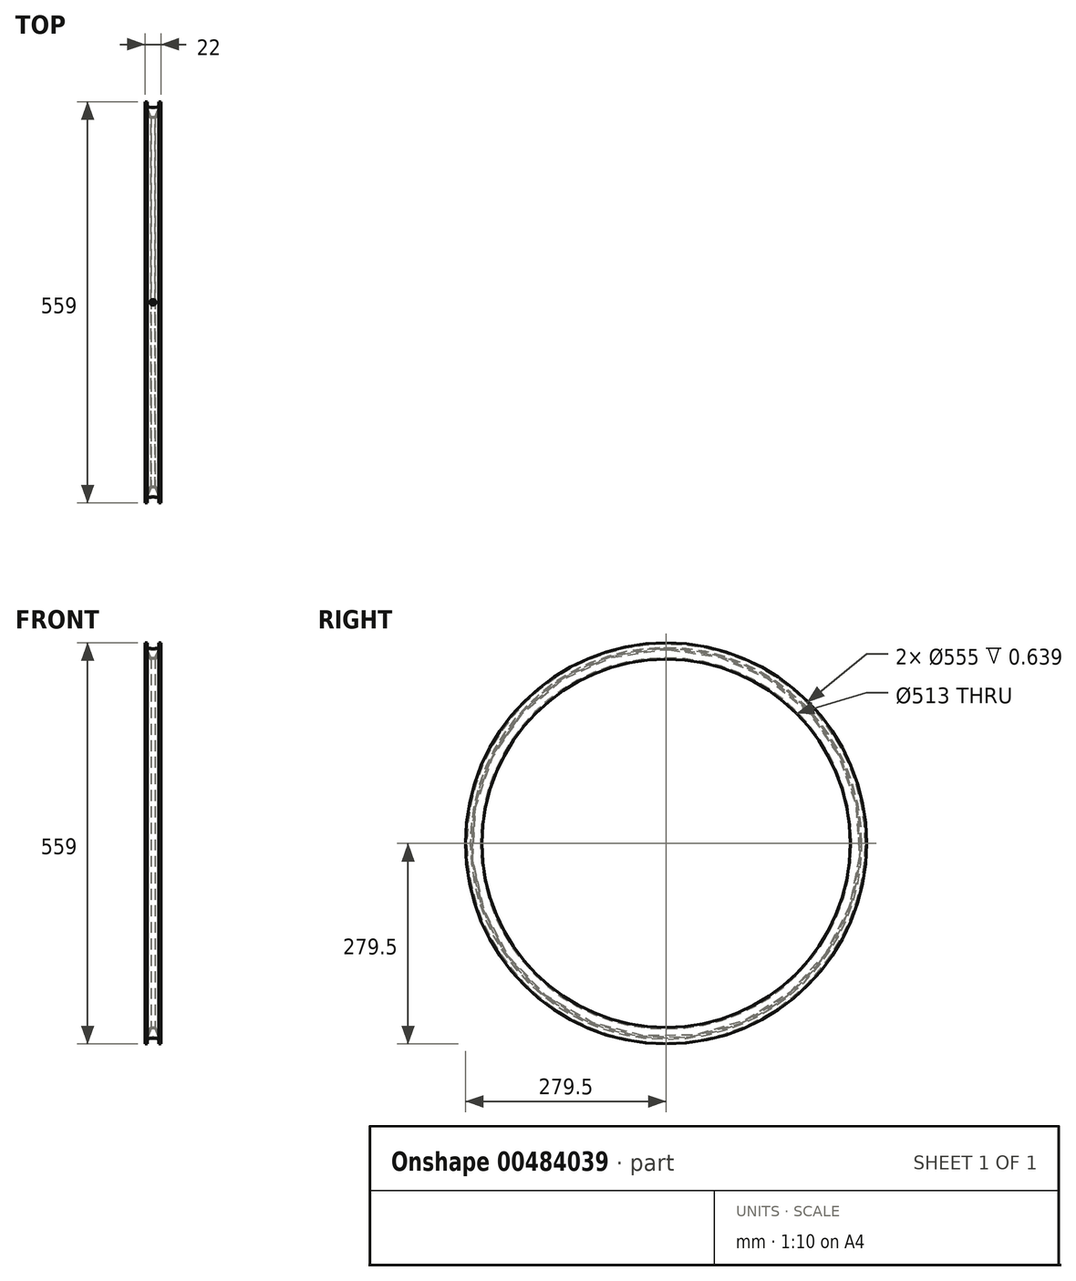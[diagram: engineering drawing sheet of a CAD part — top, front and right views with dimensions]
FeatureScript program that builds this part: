
annotation { "Feature Type Name" : "Feature", "Feature Type Description" : "" }
export const myFeature = defineFeature(function(context is Context, id is Id, definition is map)
    precondition{}
    {
        {
            var Q0;
            Q0=qCreatedBy(makeId("Front.planeOp"),FACE);
            var sketch = newSketch(context, id + "F0", { "sketchPlane" : qUnion([Q0])});
            skLineSegment(sketch, "E0", {"start": v(0, 0) * mm, "end": v(32.12, 0) * mm, "construction": true});
            skLineSegment(sketch, "E1", {"start": v(-11, 279.5) * mm, "end": v(-8, 279.5) * mm});
            skLineSegment(sketch, "E2", {"start": v(0, 279.5) * mm, "end": v(0, 0) * mm, "construction": true});
            skLineSegment(sketch, "E3", {"start": v(-11, 279.5) * mm, "end": v(-9.1, 268.15) * mm});
            skLineSegment(sketch, "E4", {"start": v(-8.73, 266.9) * mm, "end": v(-4.53, 257.67) * mm});
            skLineSegment(sketch, "E5", {"start": v(-2.71, 256.5) * mm, "end": v(2.71, 256.5) * mm});
            skLineSegment(sketch, "E6", {"start": v(4.53, 257.67) * mm, "end": v(8.73, 266.9) * mm});
            skLineSegment(sketch, "E7", {"start": v(9.1, 268.15) * mm, "end": v(11, 279.5) * mm});
            skPoint(sketch, "E8.visualSharp", {"position": v(-9, 267.5) * mm});
            skArc(sketch, "E8.filletArc", {"start": v(-9.1, 268.15) * mm, "mid": v(-8.96, 267.51) * mm, "end": v(-8.73, 266.9) * mm});
            skPoint(sketch, "E9.visualSharp", {"position": v(9, 267.5) * mm});
            skArc(sketch, "E9.filletArc", {"start": v(8.73, 266.9) * mm, "mid": v(8.96, 267.51) * mm, "end": v(9.1, 268.15) * mm});
            skPoint(sketch, "E10.visualSharp", {"position": v(-4, 256.5) * mm});
            skArc(sketch, "E10.filletArc", {"start": v(-4.53, 257.67) * mm, "mid": v(-3.8, 256.82) * mm, "end": v(-2.71, 256.5) * mm});
            skPoint(sketch, "E11.visualSharp", {"position": v(4, 256.5) * mm});
            skArc(sketch, "E11.filletArc", {"start": v(2.71, 256.5) * mm, "mid": v(3.8, 256.82) * mm, "end": v(4.53, 257.67) * mm});
            skLineSegment(sketch, "E12.0", {"start": v(-8.64, 277.5) * mm, "end": v(-8, 277.5) * mm});
            skLineSegment(sketch, "E12.1", {"start": v(7.14, 268.48) * mm, "end": v(7.57, 271.1) * mm});
            skLineSegment(sketch, "E12.2", {"start": v(-8.64, 277.5) * mm, "end": v(-7.85, 272.76) * mm});
            skArc(sketch, "E12.3", {"start": v(6.9, 267.73) * mm, "mid": v(7.05, 268.1) * mm, "end": v(7.14, 268.48) * mm});
            skLineSegment(sketch, "E12.4", {"start": v(2.71, 258.5) * mm, "end": v(6.9, 267.73) * mm});
            skLineSegment(sketch, "E12.5", {"start": v(2.71, 258.5) * mm, "end": v(2.71, 258.5) * mm});
            skArc(sketch, "E12.6", {"start": v(-7.14, 268.48) * mm, "mid": v(-7.05, 268.1) * mm, "end": v(-6.9, 267.73) * mm});
            skLineSegment(sketch, "E12.7", {"start": v(-6.9, 267.73) * mm, "end": v(-2.71, 258.5) * mm});
            skLineSegment(sketch, "E12.8", {"start": v(-2.71, 258.5) * mm, "end": v(-2.71, 258.5) * mm});
            skLineSegment(sketch, "E12.9", {"start": v(-2.71, 258.5) * mm, "end": v(2.71, 258.5) * mm});
            skLineSegment(sketch, "E13", {"start": v(-8, 279.5) * mm, "end": v(-8, 277.5) * mm});
            skLineSegment(sketch, "E14", {"start": v(8, 279.5) * mm, "end": v(8, 277.5) * mm});
            skLineSegment(sketch, "E15.trimOffspring", {"start": v(8, 279.5) * mm, "end": v(11, 279.5) * mm});
            skLineSegment(sketch, "E16.trimOffspring", {"start": v(8, 277.5) * mm, "end": v(8.64, 277.5) * mm});
            skArc(sketch, "E17", {"start": v(-7.85, 272.76) * mm, "mid": v(0, 271.5) * mm, "end": v(7.85, 272.76) * mm});
            skArc(sketch, "E18", {"start": v(-7.57, 271.1) * mm, "mid": v(0, 270) * mm, "end": v(7.57, 271.1) * mm});
            skLineSegment(sketch, "E19.trimOffspring", {"start": v(7.85, 272.76) * mm, "end": v(8.64, 277.5) * mm});
            skLineSegment(sketch, "E20.trimOffspring", {"start": v(-7.57, 271.1) * mm, "end": v(-7.14, 268.48) * mm});
            skSolve(sketch);
        }
        {
            var Q0;
            Q0 = qSketchRegion(id + "F0", true);
            var Q1;
            Q1=sQuery(id+"F0.wireOp",EDGE,"E0");
            revolve(context, id + "F1", {"entities" : qUnion([Q0]), "axis" : qUnion([Q1]), "revolveType" : RevolveType.FULL});
        }
        {
            var Q0;
            Q0=qCreatedBy(makeId("Front.planeOp"),FACE);
            var sketch = newSketch(context, id + "F2", { "sketchPlane" : qUnion([Q0])});
            skLineSegment(sketch, "E21.bottom", {"start": v(0, 250) * mm, "end": v(-2, 250) * mm});
            skLineSegment(sketch, "E21.left", {"start": v(0, 250) * mm, "end": v(0, 265) * mm});
            skLineSegment(sketch, "E21.right", {"start": v(-2, 250) * mm, "end": v(-2, 265) * mm});
            skLineSegment(sketch, "E22.bottom", {"start": v(-2, 265) * mm, "end": v(-4, 265) * mm});
            skLineSegment(sketch, "E22.top", {"start": v(0, 275) * mm, "end": v(-4, 275) * mm});
            skLineSegment(sketch, "E22.left", {"start": v(0, 265) * mm, "end": v(0, 275) * mm});
            skLineSegment(sketch, "E22.right", {"start": v(-4, 265) * mm, "end": v(-4, 275) * mm});
            skSolve(sketch);
        }
        {
            var Q0;
            Q0=qCreatedBy(makeId("Front.planeOp"),FACE);
            var sketch = newSketch(context, id + "F3", { "sketchPlane" : qUnion([Q0])});
            skLineSegment(sketch, "E23", {"start": v(0, 0) * mm, "end": v(24.44, 0) * mm, "construction": true});
            skSolve(sketch);
        }
        {
            var Q0;
            Q0 = qSketchRegion(id + "F2", true);
            var Q1;
            Q1=sQuery(id+"F2.wireOp",EDGE,"E22.left");
            revolve(context, id + "F4", {"operationType" : NewBodyOperationType.REMOVE, "entities" : qUnion([Q0]), "axis" : qUnion([Q1]), "revolveType" : RevolveType.FULL, "oppositeDirection" : true});
        }
    });
